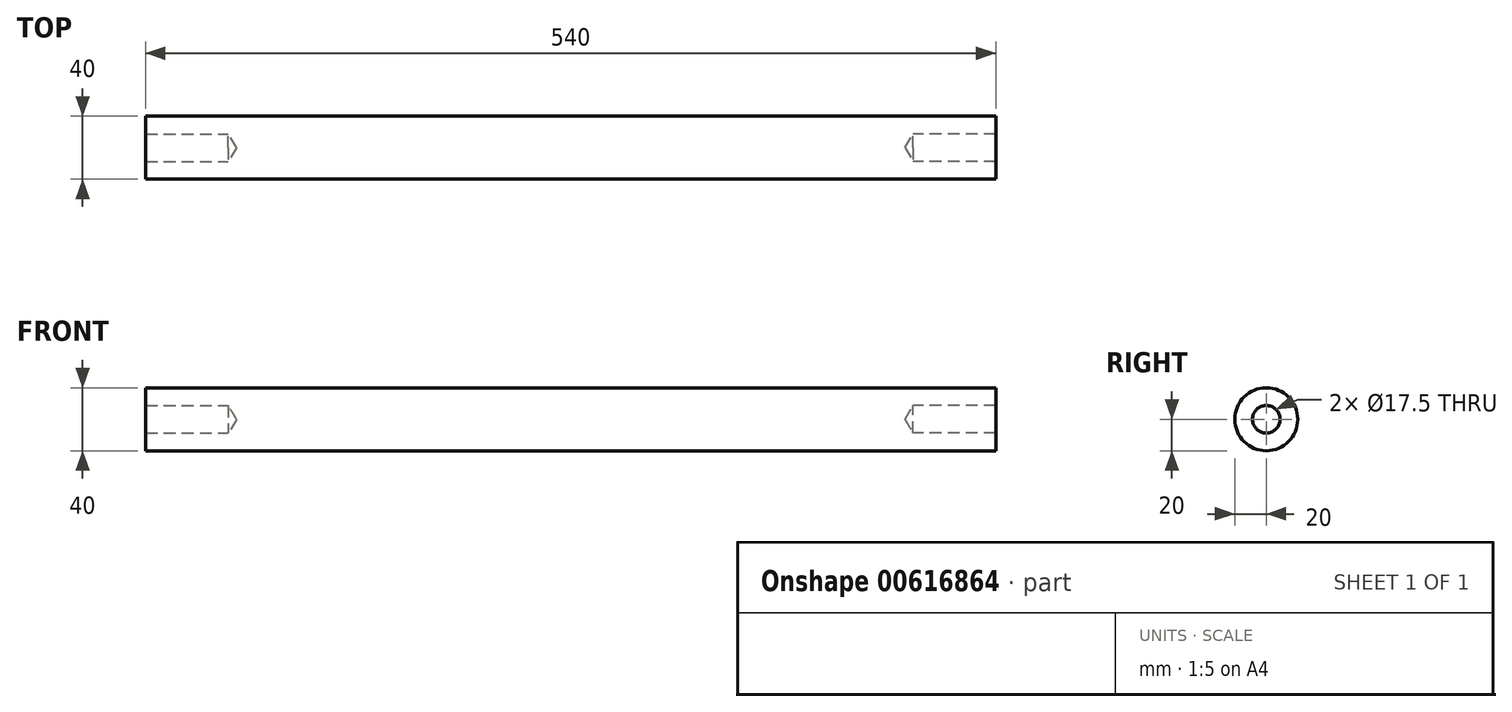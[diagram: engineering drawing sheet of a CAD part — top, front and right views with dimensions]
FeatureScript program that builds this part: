
annotation { "Feature Type Name" : "Feature", "Feature Type Description" : "" }
export const myFeature = defineFeature(function(context is Context, id is Id, definition is map)
    precondition{}
    {
        {
            var Q0;
            Q0=qCreatedBy(makeId("Right.planeOp"),FACE);
            var sketch = newSketch(context, id + "F0", { "sketchPlane" : qUnion([Q0])});
            skCircle(sketch, "E0", {"center": v(0, 0) * mm, "radius": 20 * mm});
            skSolve(sketch);
        }
        {
            var Q0;
            Q0=qSketchRegion(id+"F0",true);
            extrude(context, id + "F1", {"entities" : qUnion([Q0]), "depth" : 540 * mm, "offsetDistance" : 25 * mm, "symmetric" : true});
        }
        {
            var Q0;
            Q0=makeQuery(id+"F1.opExtrude","CAP_FACE",FACE,{"disambiguationData":[OSD([sQuery(id+"F0.wireOp",EDGE,"E0")])],"isStart":false});
            var sketch = newSketch(context, id + "F2", { "sketchPlane" : qUnion([Q0])});
            skPoint(sketch, "E1.0", {"position": v(0, 0) * mm});
            skSolve(sketch);
        }
        {
            var Q0;
            Q0=makeQuery(id+"F1.opExtrude","CAP_FACE",FACE,{"disambiguationData":[OSD([sQuery(id+"F0.wireOp",EDGE,"E0")])],"isStart":true});
            var sketch = newSketch(context, id + "F3", { "sketchPlane" : qUnion([Q0])});
            skCircle(sketch, "E2.0", {"center": v(0, 0) * mm, "radius": 20 * mm, "construction": true});
            skSolve(sketch);
        }
        {
            var Q0;
            Q0=sQuery(id+"F2.wireOp",VERTEX,"E1.0");
            var Q1;
            Q1=sQuery(id+"F3.wireOp",VERTEX,"E2.0.center");
            var Q2;
            Q2=makeQuery(id+"F1.opExtrude","SWEPT_BODY",BODY,{"disambiguationData":[OSD([sQuery(id+"F0.wireOp",EDGE,"E0")])]});
            hole(context, id + "F4", {"style" : HoleStyle.SIMPLE, "endStyle" : HoleEndStyle.BLIND, "standardTappedOrClearance" : lookupTablePath({ "standard" : "ISO", "engagement" : "75%", "pitch" : "2.5 mm", "size" : "M20", "type" : "Tapped" }), "standardBlindInLast" : lookupTablePath({ "standard" : "ISO", "engagement" : "75%", "pitch" : "2.5 mm", "size" : "M20", "type" : "Tapped" }), "holeDiameter" : 17.5 * mm, "majorDiameter" : 20 * mm, "showTappedDepth" : true, "holeDepth" : 52.5 * mm, "isTappedThrough" : true, "tappedDepth" : 40 * mm, "tapClearance" : 5, "locations" : qUnion([Q0, Q1]), "scope" : qUnion([Q2]), "startStyle" : HoleStartStyle.PART});
        }
    });
